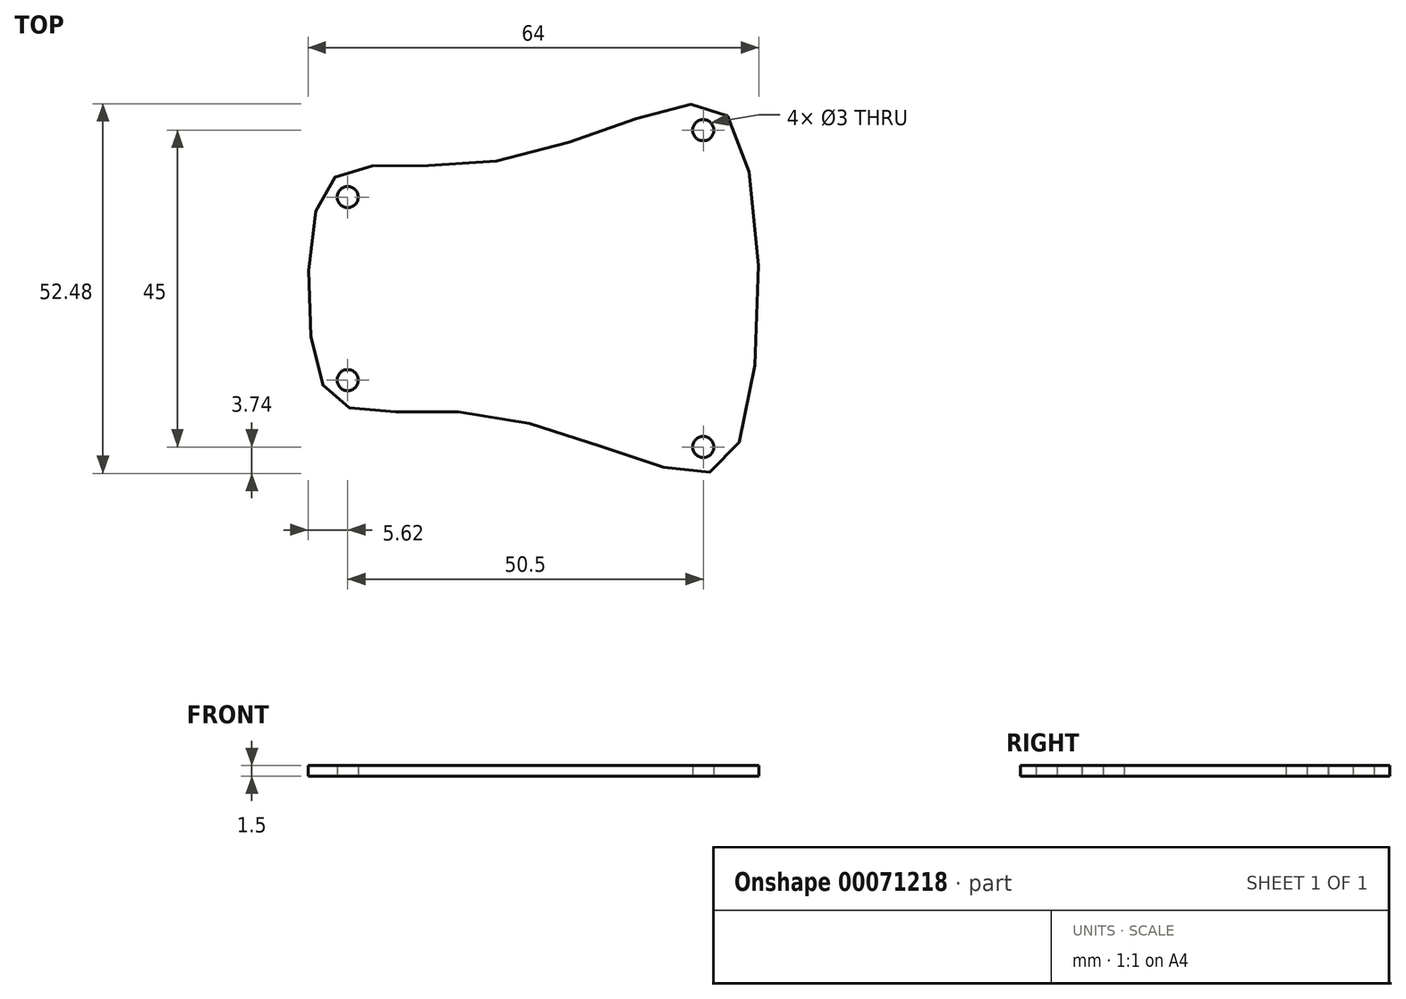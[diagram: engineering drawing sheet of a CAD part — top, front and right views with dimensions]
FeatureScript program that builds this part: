
annotation { "Feature Type Name" : "Feature", "Feature Type Description" : "" }
export const myFeature = defineFeature(function(context is Context, id is Id, definition is map)
    precondition{}
    {
        {
            var Q0;
            Q0=qCreatedBy(makeId("Top.planeOp"),FACE);
            var sketch = newSketch(context, id + "F0", { "sketchPlane" : qUnion([Q0])});
            skPoint(sketch, "E0.middle", {"position": v(0, 0) * mm});
            skCircle(sketch, "E1", {"center": v(-25.5, 13) * mm, "radius": 1.5 * mm});
            skCircle(sketch, "E2.MirrorC", {"center": v(-25.5, -13) * mm, "radius": 1.5 * mm});
            skCircle(sketch, "E3", {"center": v(25, 22.5) * mm, "radius": 1.5 * mm});
            skCircle(sketch, "E4.MirrorC", {"center": v(25, -22.5) * mm, "radius": 1.5 * mm});
            skFitSpline(sketch, "E5", {"points": [v(-30, 11) * mm, v(-25, 17) * mm, v(-5, 18) * mm, v(22, 26) * mm, v(30, 22) * mm, v(30, -22) * mm, v(22, -26) * mm, v(-5, -18) * mm, v(-25, -17) * mm, v(-30, -11) * mm, v(-30, 11) * mm]});
            skSolve(sketch);
        }
        {
            var Q0;
            Q0 = qSketchRegion(id + "F0", true);
            extrude(context, id + "F1", {"entities" : qUnion([Q0]), "depth" : 1.5 * mm});
        }
    });
